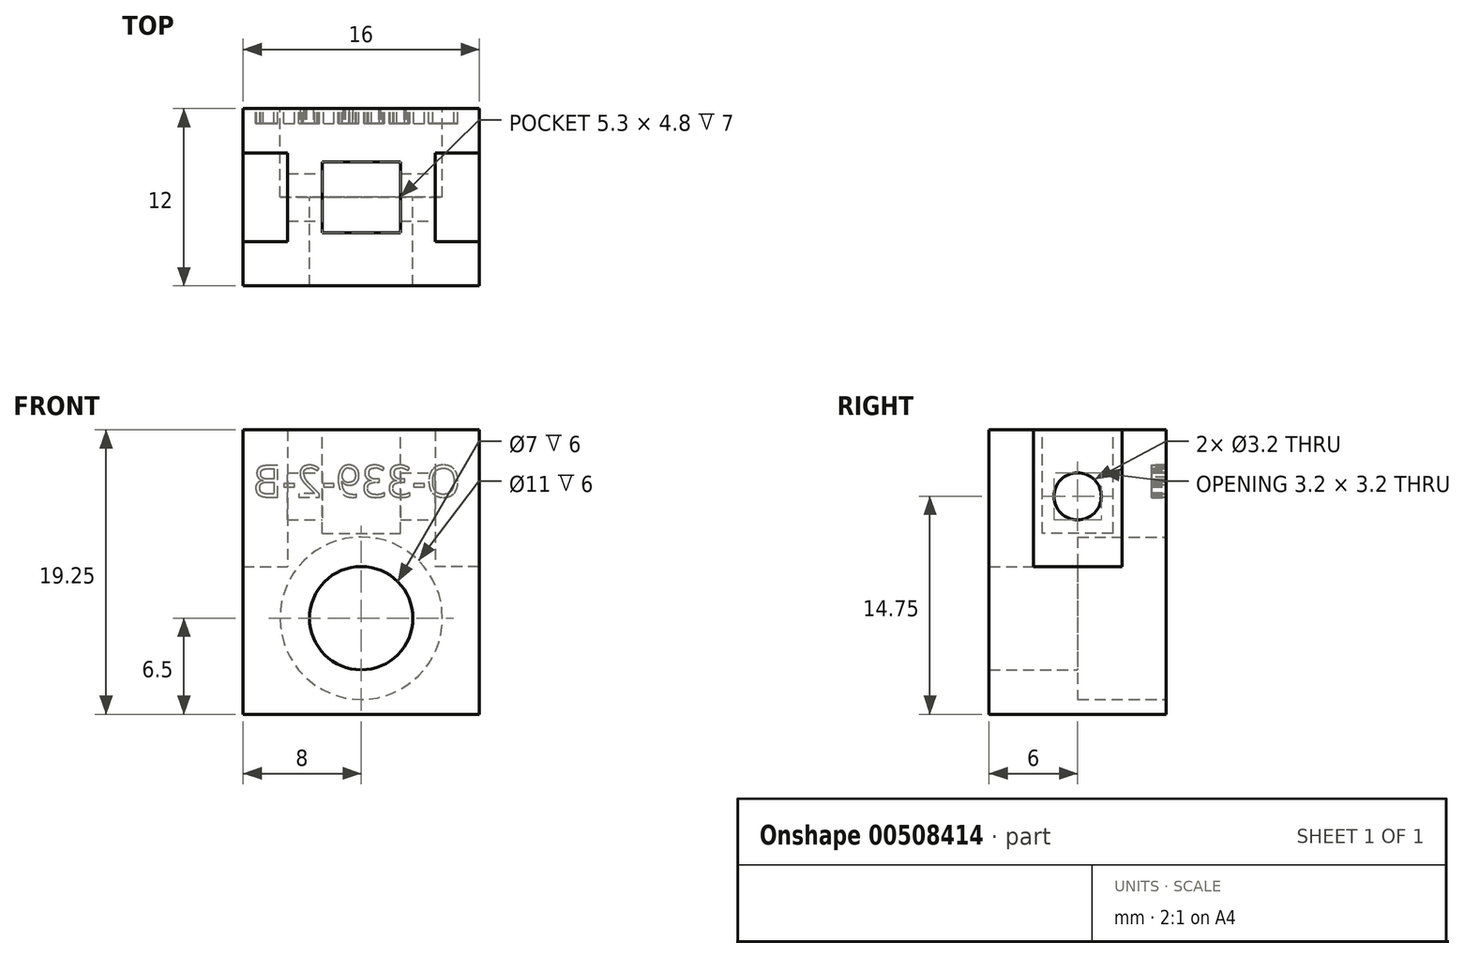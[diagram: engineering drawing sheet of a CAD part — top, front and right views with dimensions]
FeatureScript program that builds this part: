
annotation { "Feature Type Name" : "Feature", "Feature Type Description" : "" }
export const myFeature = defineFeature(function(context is Context, id is Id, definition is map)
    precondition{}
    {
        {
            var Q0;
            Q0=qCreatedBy(makeId("Top.planeOp"),FACE);
            var sketch = newSketch(context, id + "F0", { "sketchPlane" : qUnion([Q0])});
            skLineSegment(sketch, "E0", {"start": v(-8, 6) * mm, "end": v(8, 6) * mm});
            skLineSegment(sketch, "E1", {"start": v(-8, -6) * mm, "end": v(8, -6) * mm});
            skLineSegment(sketch, "E2", {"start": v(8, 6) * mm, "end": v(8, 3) * mm});
            skLineSegment(sketch, "E3", {"start": v(-8, 6) * mm, "end": v(-8, 3) * mm});
            skLineSegment(sketch, "E4", {"start": v(-8, -6) * mm, "end": v(-8, -3) * mm});
            skLineSegment(sketch, "E5", {"start": v(8, -6) * mm, "end": v(8, -3) * mm});
            skLineSegment(sketch, "E6", {"start": v(8, 3) * mm, "end": v(5, 3) * mm});
            skLineSegment(sketch, "E7", {"start": v(8, -3) * mm, "end": v(5, -3) * mm});
            skLineSegment(sketch, "E8", {"start": v(-8, 3) * mm, "end": v(-5, 3) * mm});
            skLineSegment(sketch, "E9", {"start": v(-8, -3) * mm, "end": v(-5, -3) * mm});
            skLineSegment(sketch, "E10", {"start": v(-5, 3) * mm, "end": v(-5, -3) * mm});
            skLineSegment(sketch, "E11", {"start": v(5, 3) * mm, "end": v(5, -3) * mm});
            skSolve(sketch);
        }
        {
            var Q0;
            Q0 = qSketchRegion(id + "F0", true);
            extrude(context, id + "F1", {"entities" : qUnion([Q0]), "depth" : 9.25 * mm});
        }
        {
            var Q0;
            Q0=makeQuery(id+"F1.opExtrude","SWEPT_FACE",FACE,{"disambiguationData":[OSD([sQuery(id+"F0.wireOp",EDGE,"E11")])]});
            var sketch = newSketch(context, id + "F2", { "sketchPlane" : qUnion([Q0])});
            skCircle(sketch, "E12", {"center": v(0, 4.75) * mm, "radius": 1.6 * mm});
            skSolve(sketch);
        }
        {
            var Q0;
            Q0 = qSketchRegion(id + "F2", true);
            extrude(context, id + "F3", {"entities" : qUnion([Q0]), "operationType" : NewBodyOperationType.REMOVE, "endBound" : BoundingType.THROUGH_ALL, "oppositeDirection" : true, "depth" : 25 * mm});
        }
        {
            var Q0;
            Q0=qCreatedBy(makeId("Front.planeOp"),FACE);
            var sketch = newSketch(context, id + "F4", { "sketchPlane" : qUnion([Q0])});
            skLineSegment(sketch, "E13.bottom", {"start": v(8, 0) * mm, "end": v(-8, 0) * mm});
            skLineSegment(sketch, "E13.top", {"start": v(8, -10) * mm, "end": v(-8, -10) * mm});
            skLineSegment(sketch, "E13.left", {"start": v(8, 0) * mm, "end": v(8, -10) * mm});
            skLineSegment(sketch, "E13.right", {"start": v(-8, 0) * mm, "end": v(-8, -10) * mm});
            skSolve(sketch);
        }
        {
            var Q0;
            Q0 = qSketchRegion(id + "F4", true);
            extrude(context, id + "F5", {"entities" : qUnion([Q0]), "operationType" : NewBodyOperationType.ADD, "depth" : 6 * mm});
        }
        {
            var Q0;
            Q0 = qSketchRegion(id + "F4", true);
            extrude(context, id + "F6", {"entities" : qUnion([Q0]), "operationType" : NewBodyOperationType.ADD, "oppositeDirection" : true, "depth" : 6 * mm});
        }
        {
            var Q0;
            Q0=makeQuery(id+"F6.boolean.opBoolean","MERGE",FACE,{"derivedFrom":[makeQuery(id+"F1.opExtrude","SWEPT_FACE",FACE,{"disambiguationData":[OSD([sQuery(id+"F0.wireOp",EDGE,"E0")])]}),makeQuery(id+"F6.opExtrude","CAP_FACE",FACE,{"disambiguationData":[OSD([sQuery(id+"F4.wireOp",EDGE,"E13.bottom"),sQuery(id+"F4.wireOp",EDGE,"E13.top"),sQuery(id+"F4.wireOp",EDGE,"E13.left"),sQuery(id+"F4.wireOp",EDGE,"E13.right")])],"isStart":false})]});
            var sketch = newSketch(context, id + "F7", { "sketchPlane" : qUnion([Q0])});
            skCircle(sketch, "E14", {"center": v(0, -3.5) * mm, "radius": 3.5 * mm});
            skSolve(sketch);
        }
        {
            var Q0;
            Q0 = qSketchRegion(id + "F7", true);
            extrude(context, id + "F8", {"entities" : qUnion([Q0]), "operationType" : NewBodyOperationType.REMOVE, "endBound" : BoundingType.THROUGH_ALL, "oppositeDirection" : true, "depth" : 25 * mm});
        }
        {
            var Q0;
            Q0=makeQuery(id+"F6.boolean.opBoolean","MERGE",FACE,{"derivedFrom":[makeQuery(id+"F1.opExtrude","SWEPT_FACE",FACE,{"disambiguationData":[OSD([sQuery(id+"F0.wireOp",EDGE,"E0")])]}),makeQuery(id+"F6.opExtrude","CAP_FACE",FACE,{"disambiguationData":[OSD([sQuery(id+"F4.wireOp",EDGE,"E13.bottom"),sQuery(id+"F4.wireOp",EDGE,"E13.top"),sQuery(id+"F4.wireOp",EDGE,"E13.left"),sQuery(id+"F4.wireOp",EDGE,"E13.right")])],"isStart":false})]});
            var sketch = newSketch(context, id + "F9", { "sketchPlane" : qUnion([Q0])});
            skCircle(sketch, "E15", {"center": v(0, -3.5) * mm, "radius": 5.5 * mm});
            skSolve(sketch);
        }
        {
            var Q0;
            Q0 = qSketchRegion(id + "F9", true);
            extrude(context, id + "F10", {"entities" : qUnion([Q0]), "operationType" : NewBodyOperationType.REMOVE, "oppositeDirection" : true, "depth" : 6 * mm});
        }
        {
            var Q0;
            Q0=makeQuery(id+"F1.opExtrude","CAP_FACE",FACE,{"disambiguationData":[OSD([sQuery(id+"F0.wireOp",EDGE,"E0"),sQuery(id+"F0.wireOp",EDGE,"E1"),sQuery(id+"F0.wireOp",EDGE,"E2"),sQuery(id+"F0.wireOp",EDGE,"E3"),sQuery(id+"F0.wireOp",EDGE,"E4"),sQuery(id+"F0.wireOp",EDGE,"E5"),sQuery(id+"F0.wireOp",EDGE,"E6"),sQuery(id+"F0.wireOp",EDGE,"E7"),sQuery(id+"F0.wireOp",EDGE,"E8"),sQuery(id+"F0.wireOp",EDGE,"E9"),sQuery(id+"F0.wireOp",EDGE,"E10"),sQuery(id+"F0.wireOp",EDGE,"E11")])],"isStart":false});
            var sketch = newSketch(context, id + "F11", { "sketchPlane" : qUnion([Q0])});
            skLineSegment(sketch, "E16.bottom", {"start": v(-2.65, 2.4) * mm, "end": v(2.65, 2.4) * mm});
            skLineSegment(sketch, "E16.top", {"start": v(-2.65, -2.4) * mm, "end": v(2.65, -2.4) * mm});
            skLineSegment(sketch, "E16.left", {"start": v(-2.65, 2.4) * mm, "end": v(-2.65, -2.4) * mm});
            skLineSegment(sketch, "E16.right", {"start": v(2.65, 2.4) * mm, "end": v(2.65, -2.4) * mm});
            skPoint(sketch, "E16.middle", {"position": v(0, 0) * mm});
            skSolve(sketch);
        }
        {
            var Q0;
            Q0 = qSketchRegion(id + "F11", true);
            extrude(context, id + "F12", {"entities" : qUnion([Q0]), "operationType" : NewBodyOperationType.REMOVE, "oppositeDirection" : true, "depth" : 7 * mm});
        }
        {
            var Q0;
            Q0=makeQuery(id+"F6.boolean.opBoolean","MERGE",FACE,{"derivedFrom":[makeQuery(id+"F1.opExtrude","SWEPT_FACE",FACE,{"disambiguationData":[OSD([sQuery(id+"F0.wireOp",EDGE,"E0")])]}),makeQuery(id+"F6.opExtrude","CAP_FACE",FACE,{"disambiguationData":[OSD([sQuery(id+"F4.wireOp",EDGE,"E13.bottom"),sQuery(id+"F4.wireOp",EDGE,"E13.top"),sQuery(id+"F4.wireOp",EDGE,"E13.left"),sQuery(id+"F4.wireOp",EDGE,"E13.right")])],"isStart":false})]});
            var sketch = newSketch(context, id + "F13", { "sketchPlane" : qUnion([Q0])});
            skText(sketch, "E17", { "text": "O-339-2-B", "fontName": "OpenSans-Regular.ttf"});
            const initialGuessF13  = {"E17": [-0.00673, 0.0047, 1, 0, 0.00216]};
            skSetInitialGuess(sketch, initialGuessF13);
            skSolve(sketch);
        }
        {
            var Q0;
            Q0 = qSketchRegion(id + "F13", true);
            extrude(context, id + "F14", {"entities" : qUnion([Q0]), "operationType" : NewBodyOperationType.REMOVE, "oppositeDirection" : true, "depth" : 1 * mm});
        }
    });
